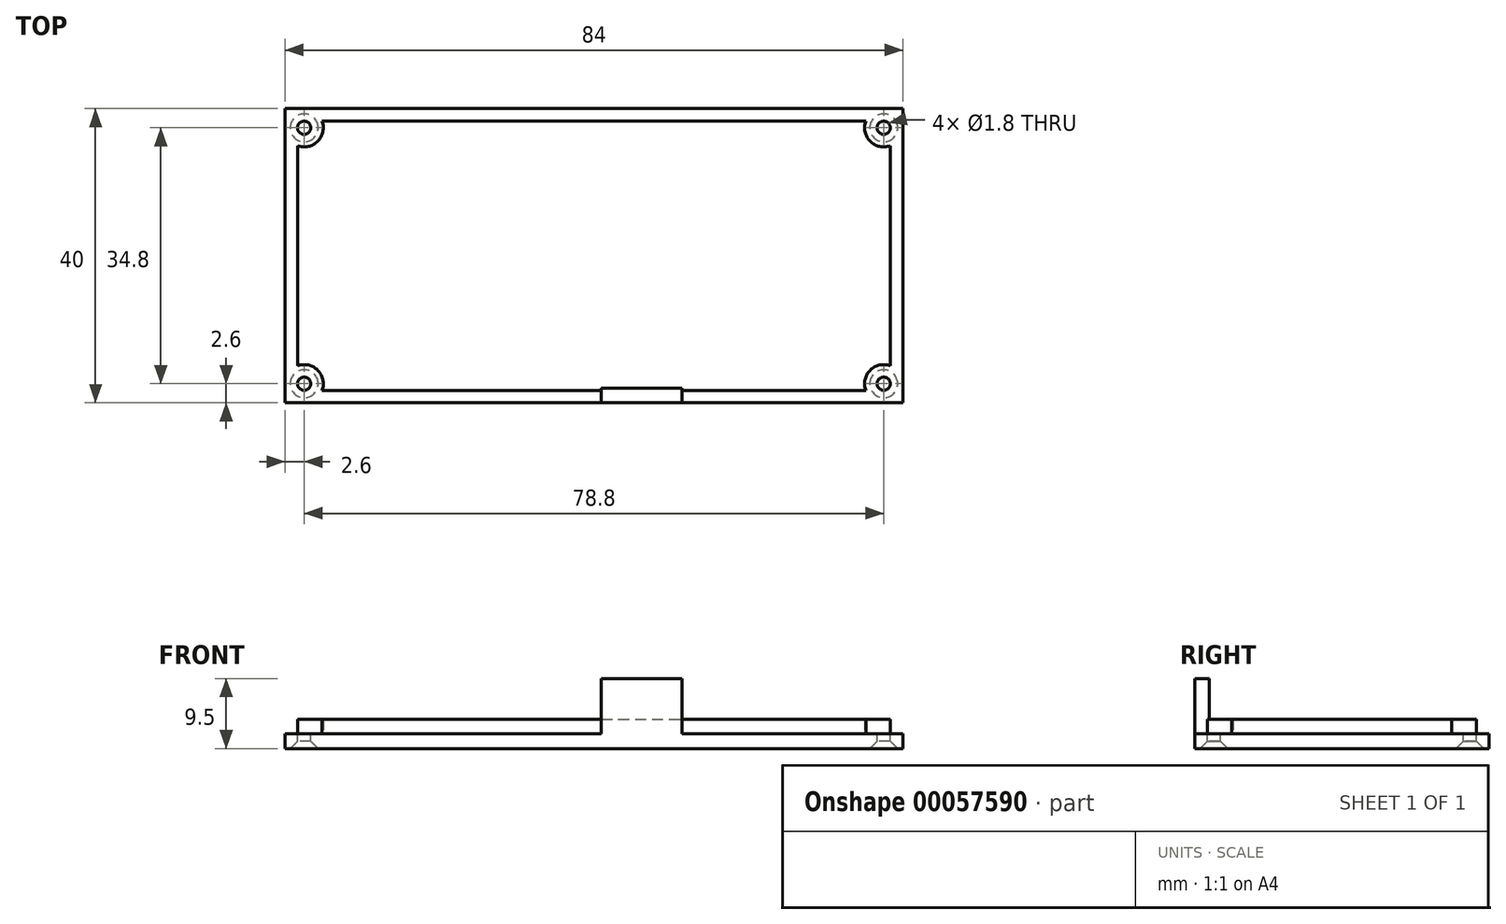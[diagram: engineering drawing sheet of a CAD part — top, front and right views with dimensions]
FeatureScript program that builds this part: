
annotation { "Feature Type Name" : "Feature", "Feature Type Description" : "" }
export const myFeature = defineFeature(function(context is Context, id is Id, definition is map)
    precondition{}
    {
        {
            var Q0;
            Q0=qCreatedBy(makeId("Top.planeOp"),FACE);
            var sketch = newSketch(context, id + "F0", { "sketchPlane" : qUnion([Q0])});
            skLineSegment(sketch, "E0.rect.bottom", {"start": v(42, -20) * mm, "end": v(-42, -20) * mm});
            skLineSegment(sketch, "E0.rect.top", {"start": v(42, 20) * mm, "end": v(-42, 20) * mm});
            skLineSegment(sketch, "E0.rect.left", {"start": v(42, -20) * mm, "end": v(42, 20) * mm});
            skLineSegment(sketch, "E0.rect.right", {"start": v(-42, -20) * mm, "end": v(-42, 20) * mm});
            skPoint(sketch, "E0.rect.middle", {"position": v(0, 0) * mm});
            skSolve(sketch);
        }
        {
            var Q0;
            Q0=makeQuery(id+"F0.imprint","IMPRINT",FACE,{"disambiguationData":[TD([[makeQuery(id+"F0.imprint","IMPRINT",EDGE,{"derivedFrom":sQuery(id+"F0.wireOp",EDGE,"E0.rect.bottom")}),-1.0]])]});
            extrude(context, id + "F1", {"entities" : qUnion([Q0]), "depth" : 2 * mm});
        }
        {
            var Q0;
            Q0=makeQuery(id+"F1.opExtrude","CAP_FACE",FACE,{"disambiguationData":[OSD([sQuery(id+"F0.wireOp",EDGE,"E0.rect.bottom"),sQuery(id+"F0.wireOp",EDGE,"E0.rect.top"),sQuery(id+"F0.wireOp",EDGE,"E0.rect.left"),sQuery(id+"F0.wireOp",EDGE,"E0.rect.right")])],"isStart":false});
            var sketch = newSketch(context, id + "F2", { "sketchPlane" : qUnion([Q0])});
            skLineSegment(sketch, "E1.rect.bottom", {"start": v(40.3, -18.3) * mm, "end": v(-40.3, -18.3) * mm});
            skLineSegment(sketch, "E1.rect.top", {"start": v(40.3, 18.3) * mm, "end": v(-40.3, 18.3) * mm});
            skLineSegment(sketch, "E1.rect.left", {"start": v(40.3, -18.3) * mm, "end": v(40.3, 18.3) * mm});
            skLineSegment(sketch, "E1.rect.right", {"start": v(-40.3, -18.3) * mm, "end": v(-40.3, 18.3) * mm});
            skCircle(sketch, "E2", {"center": v(-39.4, 17.4) * mm, "radius": 2.6 * mm});
            skCircle(sketch, "E3", {"center": v(39.4, 17.4) * mm, "radius": 2.6 * mm});
            skCircle(sketch, "E4", {"center": v(39.4, -17.4) * mm, "radius": 2.6 * mm});
            skCircle(sketch, "E5", {"center": v(-39.4, -17.4) * mm, "radius": 2.6 * mm});
            skSolve(sketch);
        }
        {
            var Q0;
            {var subQ0=sQuery(id+"F2.wireOp",EDGE,"E4");var subQ13=sQuery(id+"F2.wireOp",EDGE,"E1.rect.bottom");var subQ14=makeQuery(id+"F2.imprint","INTERSECT",VERTEX,{"derivedFrom":[subQ13,subQ0]});Q0=makeQuery(id+"F2.imprint","IMPRINT",FACE,{"disambiguationData":[TD([[makeQuery(id+"F2.imprint","IMPRINT",EDGE,{"disambiguationData":[TD([[subQ14,-1.0]])],"derivedFrom":subQ13}),-1.0]])]});}
            extrude(context, id + "F3", {"entities" : qUnion([Q0]), "operationType" : NewBodyOperationType.ADD, "depth" : 2 * mm});
        }
        {
            var Q0;
            Q0=makeQuery(id+"F1.opExtrude","CAP_FACE",FACE,{"disambiguationData":[OSD([sQuery(id+"F0.wireOp",EDGE,"E0.rect.bottom"),sQuery(id+"F0.wireOp",EDGE,"E0.rect.top"),sQuery(id+"F0.wireOp",EDGE,"E0.rect.left"),sQuery(id+"F0.wireOp",EDGE,"E0.rect.right"),sQuery(id+"F0.wireOp",EDGE,"32aea2f1-75a2-4b71-8931-6b1d8717eded.rect.bottom"),sQuery(id+"F0.wireOp",EDGE,"32aea2f1-75a2-4b71-8931-6b1d8717eded.rect.top"),sQuery(id+"F0.wireOp",EDGE,"32aea2f1-75a2-4b71-8931-6b1d8717eded.rect.left"),sQuery(id+"F0.wireOp",EDGE,"32aea2f1-75a2-4b71-8931-6b1d8717eded.rect.right")])],"isStart":false});
            var sketch = newSketch(context, id + "F4", { "sketchPlane" : qUnion([Q0])});
            skCircle(sketch, "E6", {"center": v(-39.4, 17.4) * mm, "radius": 0.9 * mm});
            skCircle(sketch, "E7", {"center": v(-39.4, -17.4) * mm, "radius": 0.9 * mm});
            skCircle(sketch, "E8", {"center": v(39.4, -17.4) * mm, "radius": 0.9 * mm});
            skCircle(sketch, "E9", {"center": v(39.4, 17.4) * mm, "radius": 0.9 * mm});
            skSolve(sketch);
        }
        {
            var Q0;
            Q0=makeQuery(id+"F1.opExtrude","SWEPT_FACE",FACE,{"disambiguationData":[OSD([sQuery(id+"F0.wireOp",EDGE,"E0.rect.bottom")])]});
            var sketch = newSketch(context, id + "F5", { "sketchPlane" : qUnion([Q0])});
            skLineSegment(sketch, "E10.top", {"start": v(-12, -20) * mm, "end": v(-1, -20) * mm});
            skLineSegment(sketch, "E10.left", {"start": v(-12, -29) * mm, "end": v(-12, -20) * mm});
            skLineSegment(sketch, "E11", {"start": v(-12, -20) * mm, "end": v(-12, 2) * mm});
            skLineSegment(sketch, "E12", {"start": v(-1, -20) * mm, "end": v(-1, 2) * mm});
            skLineSegment(sketch, "E13.bottom", {"start": v(1, 2) * mm, "end": v(12, 2) * mm});
            skLineSegment(sketch, "E13.top", {"start": v(1, 9.5) * mm, "end": v(12, 9.5) * mm});
            skLineSegment(sketch, "E13.left", {"start": v(1, 2) * mm, "end": v(1, 9.5) * mm});
            skLineSegment(sketch, "E13.right", {"start": v(12, 2) * mm, "end": v(12, 9.5) * mm});
            skSolve(sketch);
        }
        {
            var Q0;
            Q0=makeQuery(id+"F4.imprint","IMPRINT",FACE,{"disambiguationData":[TD([[makeQuery(id+"F4.imprint","IMPRINT",EDGE,{"derivedFrom":sQuery(id+"F4.wireOp",EDGE,"E6")}),1.0]])]});
            var Q1;
            Q1=makeQuery(id+"F4.imprint","IMPRINT",FACE,{"disambiguationData":[TD([[makeQuery(id+"F4.imprint","IMPRINT",EDGE,{"derivedFrom":sQuery(id+"F4.wireOp",EDGE,"E7")}),1.0]])]});
            var Q2;
            Q2=makeQuery(id+"F4.imprint","IMPRINT",FACE,{"disambiguationData":[TD([[makeQuery(id+"F4.imprint","IMPRINT",EDGE,{"derivedFrom":sQuery(id+"F4.wireOp",EDGE,"E8")}),1.0]])]});
            var Q3;
            Q3=makeQuery(id+"F4.imprint","IMPRINT",FACE,{"disambiguationData":[TD([[makeQuery(id+"F4.imprint","IMPRINT",EDGE,{"derivedFrom":sQuery(id+"F4.wireOp",EDGE,"E9")}),1.0]])]});
            extrude(context, id + "F6", {"entities" : qUnion([Q0, Q1, Q2, Q3]), "operationType" : NewBodyOperationType.REMOVE, "endBound" : BoundingType.THROUGH_ALL, "oppositeDirection" : true, "depth" : 25 * mm});
        }
        {
            var Q0;
            Q0=makeQuery(id+"F6.boolean.opBoolean","INTERSECT",EDGE,{"derivedFrom":[makeQuery(id+"F1.opExtrude","CAP_FACE",FACE,{"disambiguationData":[OSD([sQuery(id+"F0.wireOp",EDGE,"E0.rect.bottom"),sQuery(id+"F0.wireOp",EDGE,"E0.rect.top"),sQuery(id+"F0.wireOp",EDGE,"E0.rect.left"),sQuery(id+"F0.wireOp",EDGE,"E0.rect.right")])],"isStart":true}),makeQuery(id+"F6.opExtrude","SWEPT_FACE",FACE,{"disambiguationData":[OSD([sQuery(id+"F4.wireOp",EDGE,"E6")])]})]});
            var Q1;
            Q1=makeQuery(id+"F6.boolean.opBoolean","INTERSECT",EDGE,{"derivedFrom":[makeQuery(id+"F1.opExtrude","CAP_FACE",FACE,{"disambiguationData":[OSD([sQuery(id+"F0.wireOp",EDGE,"E0.rect.bottom"),sQuery(id+"F0.wireOp",EDGE,"E0.rect.top"),sQuery(id+"F0.wireOp",EDGE,"E0.rect.left"),sQuery(id+"F0.wireOp",EDGE,"E0.rect.right")])],"isStart":true}),makeQuery(id+"F6.opExtrude","SWEPT_FACE",FACE,{"disambiguationData":[OSD([sQuery(id+"F4.wireOp",EDGE,"E7")])]})]});
            var Q2;
            Q2=makeQuery(id+"F6.boolean.opBoolean","INTERSECT",EDGE,{"derivedFrom":[makeQuery(id+"F1.opExtrude","CAP_FACE",FACE,{"disambiguationData":[OSD([sQuery(id+"F0.wireOp",EDGE,"E0.rect.bottom"),sQuery(id+"F0.wireOp",EDGE,"E0.rect.top"),sQuery(id+"F0.wireOp",EDGE,"E0.rect.left"),sQuery(id+"F0.wireOp",EDGE,"E0.rect.right")])],"isStart":true}),makeQuery(id+"F6.opExtrude","SWEPT_FACE",FACE,{"disambiguationData":[OSD([sQuery(id+"F4.wireOp",EDGE,"E8")])]})]});
            var Q3;
            Q3=makeQuery(id+"F6.boolean.opBoolean","INTERSECT",EDGE,{"derivedFrom":[makeQuery(id+"F1.opExtrude","CAP_FACE",FACE,{"disambiguationData":[OSD([sQuery(id+"F0.wireOp",EDGE,"E0.rect.bottom"),sQuery(id+"F0.wireOp",EDGE,"E0.rect.top"),sQuery(id+"F0.wireOp",EDGE,"E0.rect.left"),sQuery(id+"F0.wireOp",EDGE,"E0.rect.right")])],"isStart":true}),makeQuery(id+"F6.opExtrude","SWEPT_FACE",FACE,{"disambiguationData":[OSD([sQuery(id+"F4.wireOp",EDGE,"E9")])]})]});
            chamfer(context, id + "F7", {"entities" : qUnion([Q0, Q1, Q2, Q3]), "width" : 1 * mm, "tangentPropagation" : true});
        }
        {
            var Q0;
            Q0=makeQuery(id+"F5.imprint","IMPRINT",FACE,{"disambiguationData":[TD([[makeQuery(id+"F5.imprint","IMPRINT",EDGE,{"derivedFrom":sQuery(id+"F5.wireOp",EDGE,"E13.bottom")}),-1.0]])]});
            extrude(context, id + "F8", {"entities" : qUnion([Q0]), "operationType" : NewBodyOperationType.ADD, "oppositeDirection" : true, "depth" : 2 * mm});
        }
    });
